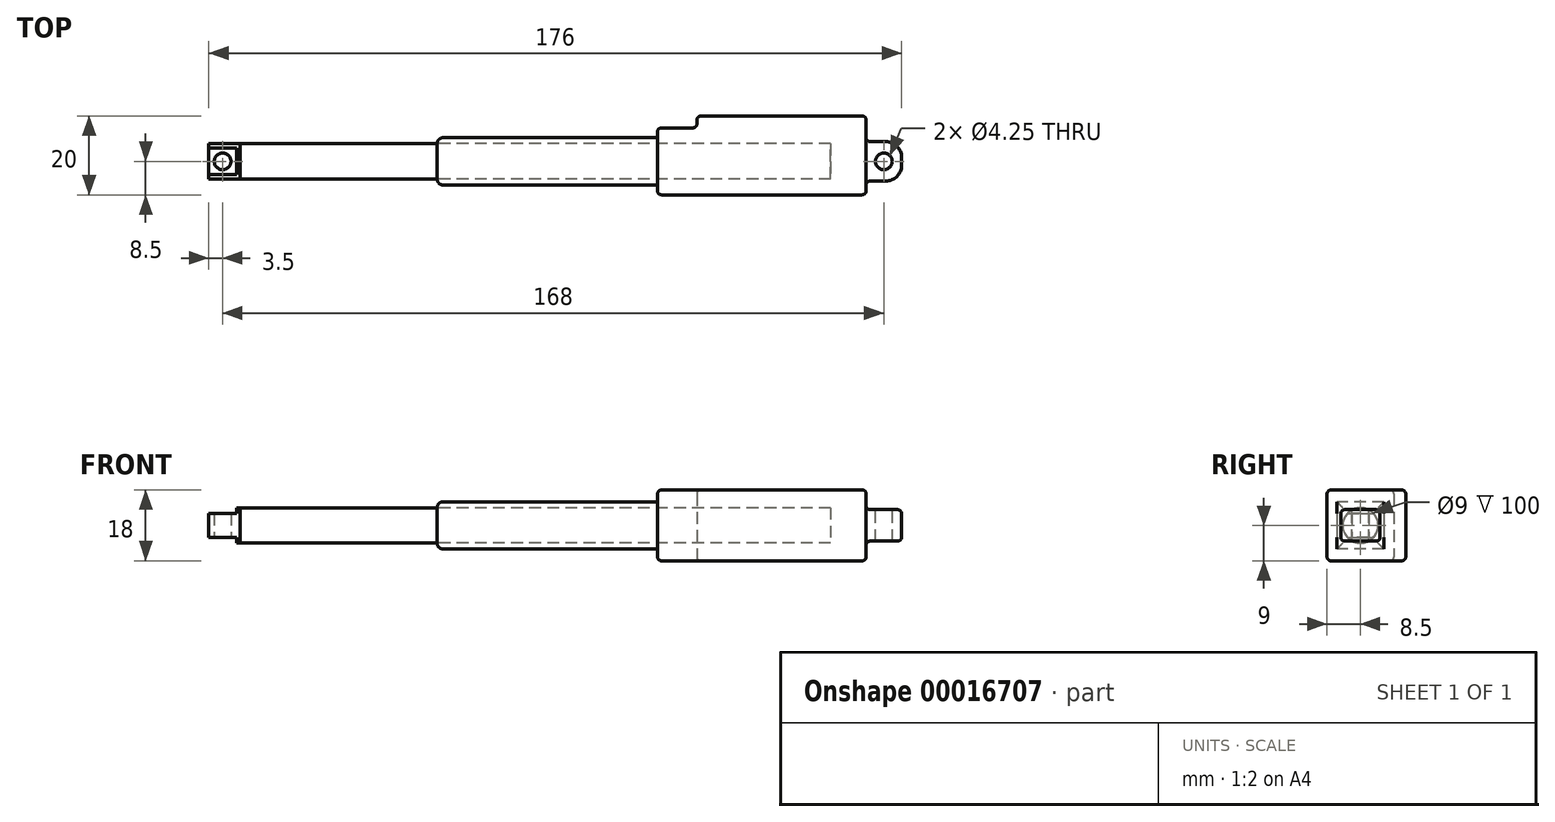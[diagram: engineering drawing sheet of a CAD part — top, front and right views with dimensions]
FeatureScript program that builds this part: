
annotation { "Feature Type Name" : "Feature", "Feature Type Description" : "" }
export const myFeature = defineFeature(function(context is Context, id is Id, definition is map)
    precondition{}
    {
        {
            var Q0;
            Q0=qCreatedBy(makeId("Right.planeOp"),FACE);
            var sketch = newSketch(context, id + "F0", { "sketchPlane" : qUnion([Q0])});
            skLineSegment(sketch, "E0.rect.bottom", {"start": v(8.5, 9) * mm, "end": v(-8.5, 9) * mm});
            skLineSegment(sketch, "E0.rect.top", {"start": v(8.5, -9) * mm, "end": v(-8.5, -9) * mm});
            skLineSegment(sketch, "E0.rect.left", {"start": v(8.5, 9) * mm, "end": v(8.5, -9) * mm});
            skLineSegment(sketch, "E0.rect.right", {"start": v(-8.5, 9) * mm, "end": v(-8.5, -9) * mm});
            skPoint(sketch, "E0.rect.middle", {"position": v(0, 0) * mm});
            skLineSegment(sketch, "E1.rect.bottom", {"start": v(5, 4) * mm, "end": v(-5, 4) * mm});
            skLineSegment(sketch, "E1.rect.top", {"start": v(5, -4) * mm, "end": v(-5, -4) * mm});
            skLineSegment(sketch, "E1.rect.left", {"start": v(5, 4) * mm, "end": v(5, -4) * mm});
            skLineSegment(sketch, "E1.rect.right", {"start": v(-5, 4) * mm, "end": v(-5, -4) * mm});
            skSolve(sketch);
        }
        {
            var Q0;
            Q0=makeQuery(id+"F0.imprint","IMPRINT",FACE,{"disambiguationData":[TD([[makeQuery(id+"F0.imprint","IMPRINT",EDGE,{"derivedFrom":sQuery(id+"F0.wireOp",EDGE,"E0.rect.bottom")}),1.0]])]});
            var Q1;
            Q1=makeQuery(id+"F0.imprint","IMPRINT",FACE,{"disambiguationData":[TD([[makeQuery(id+"F0.imprint","IMPRINT",EDGE,{"derivedFrom":sQuery(id+"F0.wireOp",EDGE,"E1.rect.bottom")}),1.0]])]});
            extrude(context, id + "F1", {"entities" : qUnion([Q0, Q1]), "oppositeDirection" : true, "depth" : 53 * mm});
        }
        {
            var Q0;
            Q0=qSketchRegion(id+"FXPcAwa9daShe2c_1",true);
            var Q1;
            Q1=makeQuery(id+"F0.imprint","IMPRINT",FACE,{"disambiguationData":[TD([[makeQuery(id+"F0.imprint","IMPRINT",EDGE,{"derivedFrom":sQuery(id+"F0.wireOp",EDGE,"E1.rect.bottom")}),1.0]])]});
            extrude(context, id + "F2", {"entities" : qUnion([Q0, Q1]), "operationType" : NewBodyOperationType.ADD, "depth" : 9 * mm});
        }
        {
            var Q0;
            Q0=makeQuery(id+"F2.opExtrude","SWEPT_FACE",FACE,{"disambiguationData":[OSD([sQuery(id+"F0.wireOp",EDGE,"E1.rect.bottom")])]});
            var sketch = newSketch(context, id + "F3", { "sketchPlane" : qUnion([Q0])});
            skCircle(sketch, "E2", {"center": v(4.5, 0) * mm, "radius": 2.12 * mm});
            skSolve(sketch);
        }
        {
            var Q0;
            Q0=makeQuery(id+"F3.imprint","IMPRINT",FACE,{"disambiguationData":[TD([[makeQuery(id+"F3.imprint","IMPRINT",EDGE,{"derivedFrom":sQuery(id+"F3.wireOp",EDGE,"E2")}),1.0]])]});
            extrude(context, id + "F4", {"entities" : qUnion([Q0]), "operationType" : NewBodyOperationType.REMOVE, "endBound" : BoundingType.THROUGH_ALL, "oppositeDirection" : true, "depth" : 25 * mm});
        }
        {
            var Q0;
            Q0=makeQuery(id+"F2.opExtrude","CAP_EDGE",EDGE,{"disambiguationData":[OSD([sQuery(id+"F0.wireOp",EDGE,"E1.rect.left")])],"isStart":false});
            var Q1;
            Q1=makeQuery(id+"F2.opExtrude","CAP_EDGE",EDGE,{"disambiguationData":[OSD([sQuery(id+"F0.wireOp",EDGE,"E1.rect.right")])],"isStart":false});
            fillet(context, id + "F5", {"entities" : qUnion([Q0, Q1]), "radius" : 4 * mm, "tangentPropagation" : true, "allowEdgeOverflow" : false});
        }
        {
            var Q0;
            Q0=makeQuery(id+"F1.opExtrude","SWEPT_FACE",FACE,{"disambiguationData":[OSD([sQuery(id+"F0.wireOp",EDGE,"E0.rect.left")])]});
            var sketch = newSketch(context, id + "F6", { "sketchPlane" : qUnion([Q0])});
            skLineSegment(sketch, "E3.0", {"start": v(43, 9) * mm, "end": v(43, -9) * mm});
            skSolve(sketch);
        }
        {
            var Q0;
            {var subQ2=sQuery(id+"F6.wireOp",EDGE,"E3.0");Q0=makeQuery(id+"F6.imprint","IMPRINT",FACE,{"disambiguationData":[TD([[makeQuery(id+"F6.imprint","IMPRINT",EDGE,{"derivedFrom":subQ2}),-1.0]])]});}
            extrude(context, id + "F7", {"entities" : qUnion([Q0]), "operationType" : NewBodyOperationType.ADD, "depth" : 3 * mm});
        }
        {
            var Q0;
            {var subQ0=sQuery(id+"F0.wireOp",EDGE,"E0.rect.bottom");Q0=makeQuery(id+"F7.boolean.opBoolean","MERGE",FACE,{"derivedFrom":[makeQuery(id+"F1.opExtrude","SWEPT_FACE",FACE,{"disambiguationData":[OSD([subQ0])]}),makeQuery(id+"F7.opExtrude","SWEPT_FACE",FACE,{"disambiguationData":[OSD([subQ0,sQuery(id+"F0.wireOp",EDGE,"E0.rect.left")])]})]});}
            var Q1;
            Q1=makeQuery(id+"F7.opExtrude","CAP_FACE",FACE,{"disambiguationData":[OSD([sQuery(id+"F0.wireOp",EDGE,"E0.rect.bottom"),sQuery(id+"F0.wireOp",EDGE,"E0.rect.top"),sQuery(id+"F0.wireOp",EDGE,"E0.rect.left"),sQuery(id+"F6.wireOp",EDGE,"E3.0")])],"isStart":false});
            var Q2;
            Q2=makeQuery(id+"F1.opExtrude","SWEPT_FACE",FACE,{"disambiguationData":[OSD([sQuery(id+"F0.wireOp",EDGE,"E0.rect.left")])]});
            var Q3;
            Q3=makeQuery(id+"F7.opExtrude","SWEPT_FACE",FACE,{"disambiguationData":[OSD([sQuery(id+"F6.wireOp",EDGE,"E3.0")])]});
            var Q4;
            {var subQ0=sQuery(id+"F0.wireOp",EDGE,"E0.rect.top");Q4=makeQuery(id+"F7.boolean.opBoolean","MERGE",FACE,{"derivedFrom":[makeQuery(id+"F1.opExtrude","SWEPT_FACE",FACE,{"disambiguationData":[OSD([subQ0])]}),makeQuery(id+"F7.opExtrude","SWEPT_FACE",FACE,{"disambiguationData":[OSD([subQ0,sQuery(id+"F0.wireOp",EDGE,"E0.rect.left")])]})]});}
            var Q5;
            Q5=makeQuery(id+"F1.opExtrude","SWEPT_FACE",FACE,{"disambiguationData":[OSD([sQuery(id+"F0.wireOp",EDGE,"E0.rect.right")])]});
            var Q6;
            {var subQ0=sQuery(id+"F0.wireOp",EDGE,"E0.rect.left");Q6=makeQuery(id+"F7.boolean.opBoolean","MERGE",FACE,{"derivedFrom":[makeQuery(id+"F1.opExtrude","CAP_FACE",FACE,{"disambiguationData":[OSD([sQuery(id+"F0.wireOp",EDGE,"E0.rect.bottom"),sQuery(id+"F0.wireOp",EDGE,"E0.rect.top"),subQ0,sQuery(id+"F0.wireOp",EDGE,"E0.rect.right")])],"isStart":true}),makeQuery(id+"F7.opExtrude","SWEPT_FACE",FACE,{"disambiguationData":[OSD([subQ0])]})]});}
            var Q7;
            Q7=makeQuery(id+"F2.opExtrude","SWEPT_EDGE",EDGE,{"disambiguationData":[OSD([sQuery(id+"F0.wireOp",EDGE,"E1.rect.bottom"),sQuery(id+"F0.wireOp",EDGE,"E1.rect.right")])]});
            var Q8;
            Q8=makeQuery(id+"F5.opFillet","BLEND_EDGE",EDGE,{"blendedFrom":[makeQuery(id+"F2.opExtrude","CAP_EDGE",EDGE,{"disambiguationData":[OSD([sQuery(id+"F0.wireOp",EDGE,"E1.rect.right")])],"isStart":false}),makeQuery(id+"F2.opExtrude","SWEPT_FACE",FACE,{"disambiguationData":[OSD([sQuery(id+"F0.wireOp",EDGE,"E1.rect.bottom")])]})],"blendedInto":[makeQuery(id+"F2.opExtrude","SWEPT_FACE",FACE,{"disambiguationData":[OSD([sQuery(id+"F0.wireOp",EDGE,"E1.rect.bottom")])]})]});
            var Q9;
            Q9=makeQuery(id+"F2.opExtrude","CAP_EDGE",EDGE,{"disambiguationData":[OSD([sQuery(id+"F0.wireOp",EDGE,"E1.rect.bottom")])],"isStart":false});
            var Q10;
            Q10=makeQuery(id+"F5.opFillet","BLEND_EDGE",EDGE,{"blendedFrom":[makeQuery(id+"F2.opExtrude","CAP_EDGE",EDGE,{"disambiguationData":[OSD([sQuery(id+"F0.wireOp",EDGE,"E1.rect.left")])],"isStart":false}),makeQuery(id+"F2.opExtrude","SWEPT_FACE",FACE,{"disambiguationData":[OSD([sQuery(id+"F0.wireOp",EDGE,"E1.rect.bottom")])]})],"blendedInto":[makeQuery(id+"F2.opExtrude","SWEPT_FACE",FACE,{"disambiguationData":[OSD([sQuery(id+"F0.wireOp",EDGE,"E1.rect.bottom")])]})]});
            var Q11;
            Q11=makeQuery(id+"F2.opExtrude","SWEPT_EDGE",EDGE,{"disambiguationData":[OSD([sQuery(id+"F0.wireOp",EDGE,"E1.rect.bottom"),sQuery(id+"F0.wireOp",EDGE,"E1.rect.left")])]});
            var Q12;
            Q12=makeQuery(id+"F2.opExtrude","SWEPT_EDGE",EDGE,{"disambiguationData":[OSD([sQuery(id+"F0.wireOp",EDGE,"E1.rect.top"),sQuery(id+"F0.wireOp",EDGE,"E1.rect.right")])]});
            var Q13;
            Q13=makeQuery(id+"F5.opFillet","BLEND_EDGE",EDGE,{"blendedFrom":[makeQuery(id+"F2.opExtrude","CAP_EDGE",EDGE,{"disambiguationData":[OSD([sQuery(id+"F0.wireOp",EDGE,"E1.rect.right")])],"isStart":false}),makeQuery(id+"F2.opExtrude","SWEPT_FACE",FACE,{"disambiguationData":[OSD([sQuery(id+"F0.wireOp",EDGE,"E1.rect.top")])]})],"blendedInto":[makeQuery(id+"F2.opExtrude","SWEPT_FACE",FACE,{"disambiguationData":[OSD([sQuery(id+"F0.wireOp",EDGE,"E1.rect.top")])]})]});
            var Q14;
            Q14=makeQuery(id+"F2.opExtrude","CAP_EDGE",EDGE,{"disambiguationData":[OSD([sQuery(id+"F0.wireOp",EDGE,"E1.rect.top")])],"isStart":false});
            var Q15;
            Q15=makeQuery(id+"F5.opFillet","BLEND_EDGE",EDGE,{"blendedFrom":[makeQuery(id+"F2.opExtrude","CAP_EDGE",EDGE,{"disambiguationData":[OSD([sQuery(id+"F0.wireOp",EDGE,"E1.rect.left")])],"isStart":false}),makeQuery(id+"F2.opExtrude","SWEPT_FACE",FACE,{"disambiguationData":[OSD([sQuery(id+"F0.wireOp",EDGE,"E1.rect.top")])]})],"blendedInto":[makeQuery(id+"F2.opExtrude","SWEPT_FACE",FACE,{"disambiguationData":[OSD([sQuery(id+"F0.wireOp",EDGE,"E1.rect.top")])]})]});
            var Q16;
            Q16=makeQuery(id+"F2.opExtrude","SWEPT_EDGE",EDGE,{"disambiguationData":[OSD([sQuery(id+"F0.wireOp",EDGE,"E1.rect.top"),sQuery(id+"F0.wireOp",EDGE,"E1.rect.left")])]});
            fillet(context, id + "F8", {"entities" : qUnion([Q0, Q1, Q2, Q3, Q4, Q5, Q6, Q7, Q8, Q9, Q10, Q11, Q12, Q13, Q14, Q15, Q16]), "radius" : 1 * mm, "allowEdgeOverflow" : false});
        }
        {
            var Q0;
            Q0=makeQuery(id+"F1.opExtrude","CAP_FACE",FACE,{"disambiguationData":[OSD([sQuery(id+"F0.wireOp",EDGE,"E0.rect.bottom"),sQuery(id+"F0.wireOp",EDGE,"E0.rect.top"),sQuery(id+"F0.wireOp",EDGE,"E0.rect.left"),sQuery(id+"F0.wireOp",EDGE,"E0.rect.right")])],"isStart":false});
            var sketch = newSketch(context, id + "F9", { "sketchPlane" : qUnion([Q0])});
            skLineSegment(sketch, "E4.rect.bottom", {"start": v(-6, 6) * mm, "end": v(6, 6) * mm});
            skLineSegment(sketch, "E4.rect.top", {"start": v(-6, -6) * mm, "end": v(6, -6) * mm});
            skLineSegment(sketch, "E4.rect.left", {"start": v(-6, 6) * mm, "end": v(-6, -6) * mm});
            skLineSegment(sketch, "E4.rect.right", {"start": v(6, 6) * mm, "end": v(6, -6) * mm});
            skPoint(sketch, "E4.rect.middle", {"position": v(0, 0) * mm});
            skSolve(sketch);
        }
        {
            var Q0;
            Q0=makeQuery(id+"F9.imprint","IMPRINT",FACE,{"disambiguationData":[TD([[makeQuery(id+"F9.imprint","IMPRINT",EDGE,{"derivedFrom":sQuery(id+"F9.wireOp",EDGE,"E4.rect.bottom")}),-1.0]])]});
            extrude(context, id + "F10", {"entities" : qUnion([Q0]), "operationType" : NewBodyOperationType.ADD, "depth" : 56 * mm});
        }
        {
            var Q0;
            Q0=makeQuery(id+"F10.opExtrude","CAP_FACE",FACE,{"disambiguationData":[OSD([sQuery(id+"F9.wireOp",EDGE,"E4.rect.bottom"),sQuery(id+"F9.wireOp",EDGE,"E4.rect.top"),sQuery(id+"F9.wireOp",EDGE,"E4.rect.left"),sQuery(id+"F9.wireOp",EDGE,"E4.rect.right")])],"isStart":false});
            fillet(context, id + "F11", {"entities" : qUnion([Q0]), "radius" : 1.5 * mm, "tangentPropagation" : true, "allowEdgeOverflow" : false});
        }
        {
            var Q0;
            Q0=makeQuery(id+"F10.opExtrude","CAP_FACE",FACE,{"disambiguationData":[OSD([sQuery(id+"F9.wireOp",EDGE,"E4.rect.bottom"),sQuery(id+"F9.wireOp",EDGE,"E4.rect.top"),sQuery(id+"F9.wireOp",EDGE,"E4.rect.left"),sQuery(id+"F9.wireOp",EDGE,"E4.rect.right")])],"isStart":false});
            var sketch = newSketch(context, id + "F12", { "sketchPlane" : qUnion([Q0])});
            skCircle(sketch, "E5", {"center": v(0, 0) * mm, "radius": 4.5 * mm});
            skSolve(sketch);
        }
        {
            var Q0;
            Q0=qSketchRegion(id+"F12",true);
            extrude(context, id + "F13", {"entities" : qUnion([Q0]), "operationType" : NewBodyOperationType.REMOVE, "oppositeDirection" : true, "depth" : 100 * mm});
        }
        {
            var Q0;
            {var subQ0=sQuery(id+"F12.wireOp",EDGE,"E5");var subQ1=sQuery(id+"F9.wireOp",EDGE,"E4.rect.top");var subQ2=sQuery(id+"F9.wireOp",EDGE,"E4.rect.bottom");var subQ3=sQuery(id+"F9.wireOp",EDGE,"E4.rect.left");var subQ4=sQuery(id+"F9.wireOp",EDGE,"E4.rect.right");var subQ5=makeQuery(id+"F10.opExtrude","CAP_FACE",FACE,{"disambiguationData":[OSD([subQ2,subQ1,subQ3,subQ4])],"isStart":false});var subQ9=makeQuery(id+"F12.imprint","INTERSECT",VERTEX,{"derivedFrom":[makeQuery(id+"F11.opFillet","BLEND_EDGE",EDGE,{"blendedFrom":[makeQuery(id+"F10.opExtrude","CAP_EDGE",EDGE,{"disambiguationData":[OSD([subQ2])],"isStart":false}),subQ5],"blendedInto":[subQ5]}),subQ0]});Q0=makeQuery(id+"F12.imprint","IMPRINT",FACE,{"disambiguationData":[TD([[makeQuery(id+"F12.imprint","IMPRINT",EDGE,{"disambiguationData":[TD([[subQ9,1.0]])],"derivedFrom":subQ0}),1.0]])]});}
            extrude(context, id + "F14", {"entities" : qUnion([Q0]), "depth" : 50 * mm});
        }
        {
            var Q0;
            Q0=makeQuery(id+"F14.opExtrude","CAP_FACE",FACE,{"disambiguationData":[OSD([sQuery(id+"F12.wireOp",EDGE,"E5")])],"isStart":false});
            extrude(context, id + "F15", {"entities" : qUnion([Q0]), "depth" : 8 * mm});
        }
        {
            var Q0;
            Q0=makeQuery(id+"F15.opExtrude","CAP_FACE",FACE,{"disambiguationData":[OSD([sQuery(id+"F12.wireOp",EDGE,"E5")])],"isStart":false});
            var sketch = newSketch(context, id + "F16", { "sketchPlane" : qUnion([Q0])});
            skLineSegment(sketch, "E6.rect.bottom", {"start": v(4.5, 3) * mm, "end": v(-4.5, 3) * mm});
            skLineSegment(sketch, "E6.rect.top", {"start": v(4.5, -3) * mm, "end": v(-4.5, -3) * mm});
            skLineSegment(sketch, "E6.rect.left", {"start": v(4.5, 3) * mm, "end": v(4.5, -3) * mm});
            skLineSegment(sketch, "E6.rect.right", {"start": v(-4.5, 3) * mm, "end": v(-4.5, -3) * mm});
            skPoint(sketch, "E6.rect.middle", {"position": v(0, 0) * mm});
            skSolve(sketch);
        }
        {
            var Q0;
            {var subQ0=makeQuery(id+"F15.opExtrude","CAP_EDGE",EDGE,{"disambiguationData":[OSD([sQuery(id+"F12.wireOp",EDGE,"E5")])],"isStart":false});var subQ1=sQuery(id+"F16.wireOp",EDGE,"E6.rect.top");var subQ3=makeQuery(id+"F16.imprint","INTERSECT",VERTEX,{"disambiguationData":[OD(0.0)],"derivedFrom":[subQ0,subQ1]});Q0=makeQuery(id+"F16.imprint","IMPRINT",FACE,{"disambiguationData":[TD([[makeQuery(id+"F16.imprint","IMPRINT",EDGE,{"disambiguationData":[TD([[subQ3,-1.0]])],"derivedFrom":subQ1}),1.0]])]});}
            var Q1;
            {var subQ0=makeQuery(id+"F15.opExtrude","CAP_EDGE",EDGE,{"disambiguationData":[OSD([sQuery(id+"F12.wireOp",EDGE,"E5")])],"isStart":false});var subQ1=sQuery(id+"F16.wireOp",EDGE,"E6.rect.bottom");var subQ3=makeQuery(id+"F16.imprint","INTERSECT",VERTEX,{"disambiguationData":[OD(0.0)],"derivedFrom":[subQ0,subQ1]});Q1=makeQuery(id+"F16.imprint","IMPRINT",FACE,{"disambiguationData":[TD([[makeQuery(id+"F16.imprint","IMPRINT",EDGE,{"disambiguationData":[TD([[subQ3,-1.0]])],"derivedFrom":subQ1}),-1.0]])]});}
            extrude(context, id + "F17", {"entities" : qUnion([Q0, Q1]), "operationType" : NewBodyOperationType.REMOVE, "oppositeDirection" : true, "depth" : 7 * mm});
        }
        {
            var Q0;
            Q0=makeQuery(id+"F17.boolean.opBoolean","COPY",FACE,{"derivedFrom":makeQuery(id+"F17.opExtrude","SWEPT_FACE",FACE,{"disambiguationData":[OSD([sQuery(id+"F16.wireOp",EDGE,"E6.rect.top")])]})});
            var sketch = newSketch(context, id + "F18", { "sketchPlane" : qUnion([Q0])});
            skCircle(sketch, "E7", {"center": v(-163.5, 0) * mm, "radius": 2.12 * mm});
            skSolve(sketch);
        }
        {
            var Q0;
            Q0=makeQuery(id+"F18.imprint","IMPRINT",FACE,{"disambiguationData":[TD([[makeQuery(id+"F18.imprint","IMPRINT",EDGE,{"derivedFrom":sQuery(id+"F18.wireOp",EDGE,"E7")}),1.0]])]});
            extrude(context, id + "F19", {"entities" : qUnion([Q0]), "operationType" : NewBodyOperationType.REMOVE, "endBound" : BoundingType.THROUGH_ALL, "oppositeDirection" : true, "depth" : 25 * mm});
        }
    });
